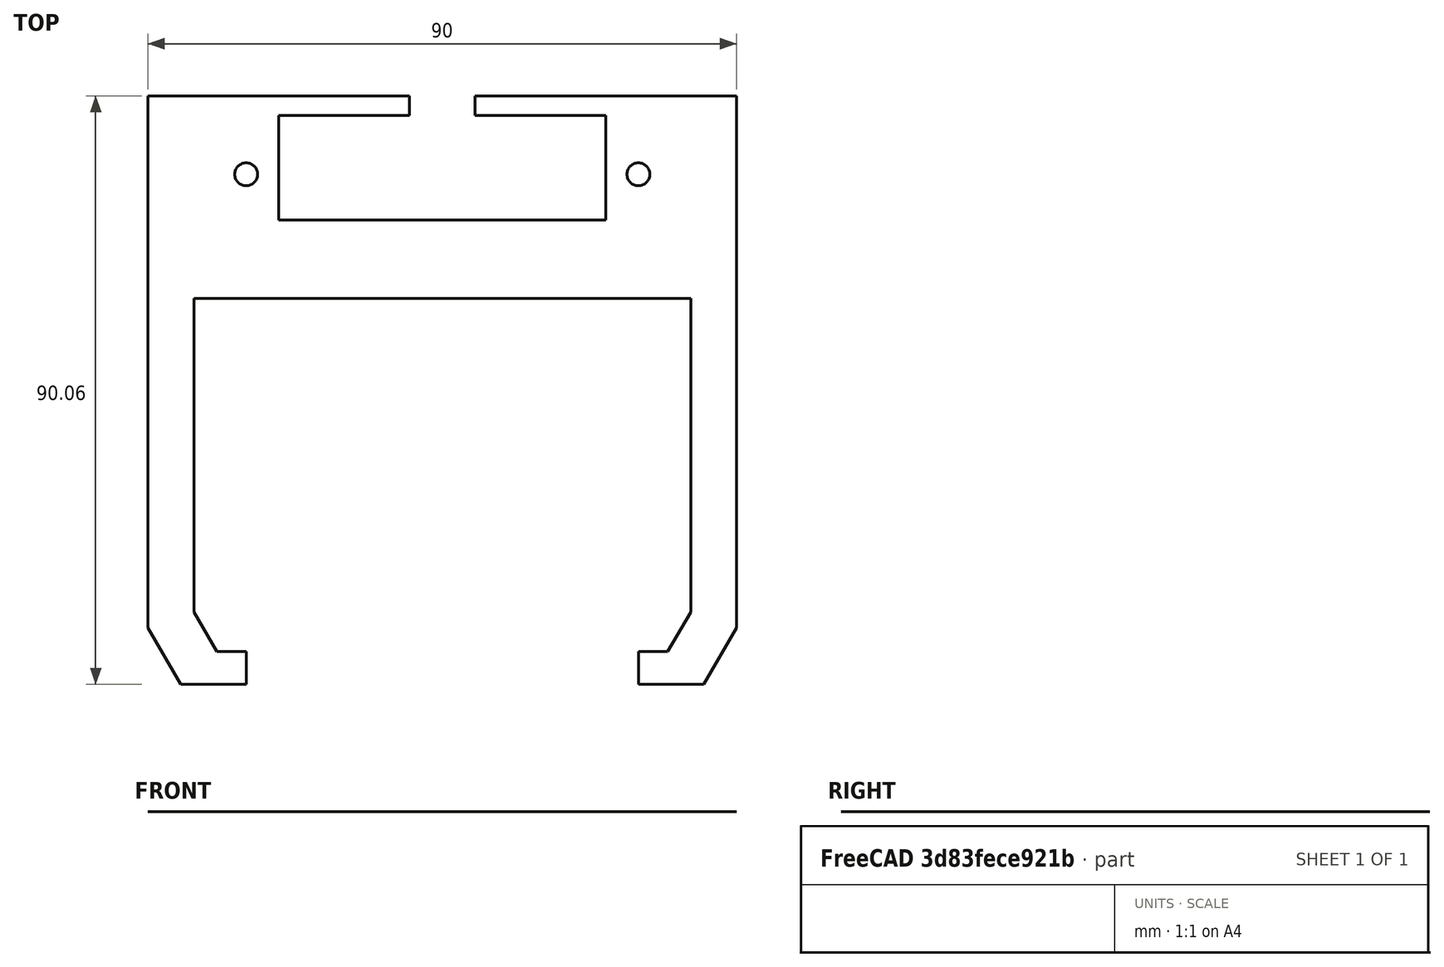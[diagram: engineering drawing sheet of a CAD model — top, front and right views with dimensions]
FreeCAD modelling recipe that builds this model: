
FCSTD DOCUMENT  (FreeCAD 2022.430R26244 +4758 (Git))
Label: as3MotorFrame
License: All rights reserved
LicenseURL: http://en.wikipedia.org/wiki/All_rights_reserved
objects: Part::FeaturePython×8, App::FeaturePython×2, App::Link×1
note: 7 computed .brp shape members not serialized (recipe doc carries the construction recipe); baked Part::Feature solids carry a one-line shape summary decoded from their .brp
EXTERNAL_REF file=motor_frame.FCStd obj=ShapeCopy

FEATURE [App::FeaturePython] Constraints  # WARN: FeaturePython — macro-defined, semantics opaque (R4)
  TreeRank = 0
  _LinkVersion = 1
  _Version = 1
FEATURE [App::Link] Link  label="MotorFrame"
  AutoLinkLabel = false
  AutoPlacement = true
  LinkedObject = -> <external motor_frame.FCStd>#ShapeCopy
  SyncGroupVisibility = false
  TreeRank = 0
  _LinkOwner = 2961
  _LinkVersion = 1
FEATURE [Part::FeaturePython] Parts  # WARN: FeaturePython — macro-defined, semantics opaque (R4)
  Group = -> [Link]
  GroupMode = 0
  TreeRank = 0
  _LinkVersion = 1
FEATURE [Part::FeaturePython] Assembly  label="As3motorFrame"  # WARN: FeaturePython — macro-defined, semantics opaque (R4)
  AutoRelax = true
  BuildShape = 0
  Freeze = false
  Group = -> [Constraints,Elements,Parts]
  TreeRank = 0
  Verbose = false
  _LinkVersion = 1
  _SolverType = 1
  _Version = 1
FEATURE [App::FeaturePython] Elements  # WARN: FeaturePython — macro-defined, semantics opaque (R4)
  Group = -> [Element,Element001,Element002,Element003,Element004,Element005]
  TreeRank = 0
  _LinkVersion = 1
FEATURE [Part::FeaturePython] Element  label="Fix1"  # link proxy (typed FeaturePython)
  Detach = false
  LinkTransform = true
  LinkedObject = -> Link [Edge127]
  TreeRank = 0
  _LinkVersion = 1
  _Parent = -> Elements
FEATURE [Part::FeaturePython] Element001  label="Fix2"  # link proxy (typed FeaturePython)
  Detach = false
  LinkTransform = true
  LinkedObject = -> Link [Edge113]
  TreeRank = 0
  _LinkVersion = 1
  _Parent = -> Elements
FEATURE [Part::FeaturePython] Element002  label="AppuiH1"  # link proxy (typed FeaturePython)
  Detach = false
  LinkTransform = true
  LinkedObject = -> Link [Face5]
  TreeRank = 0
  _LinkVersion = 1
  _Parent = -> Elements
FEATURE [Part::FeaturePython] Element003  label="Fix3"  # link proxy (typed FeaturePython)
  Detach = false
  LinkTransform = true
  LinkedObject = -> Link [Edge53]
  TreeRank = 0
  _LinkVersion = 1
  _Parent = -> Elements
FEATURE [Part::FeaturePython] Element004  label="Fix4"  # link proxy (typed FeaturePython)
  Detach = false
  LinkTransform = true
  LinkedObject = -> Link [Edge54]
  TreeRank = 0
  _LinkVersion = 1
  _Parent = -> Elements
FEATURE [Part::FeaturePython] Element005  label="CentrMot"  # link proxy (typed FeaturePython)
  Detach = false
  LinkTransform = true
  LinkedObject = -> Link [Edge63]
  TreeRank = 0
  _LinkVersion = 1
  _Parent = -> Elements
